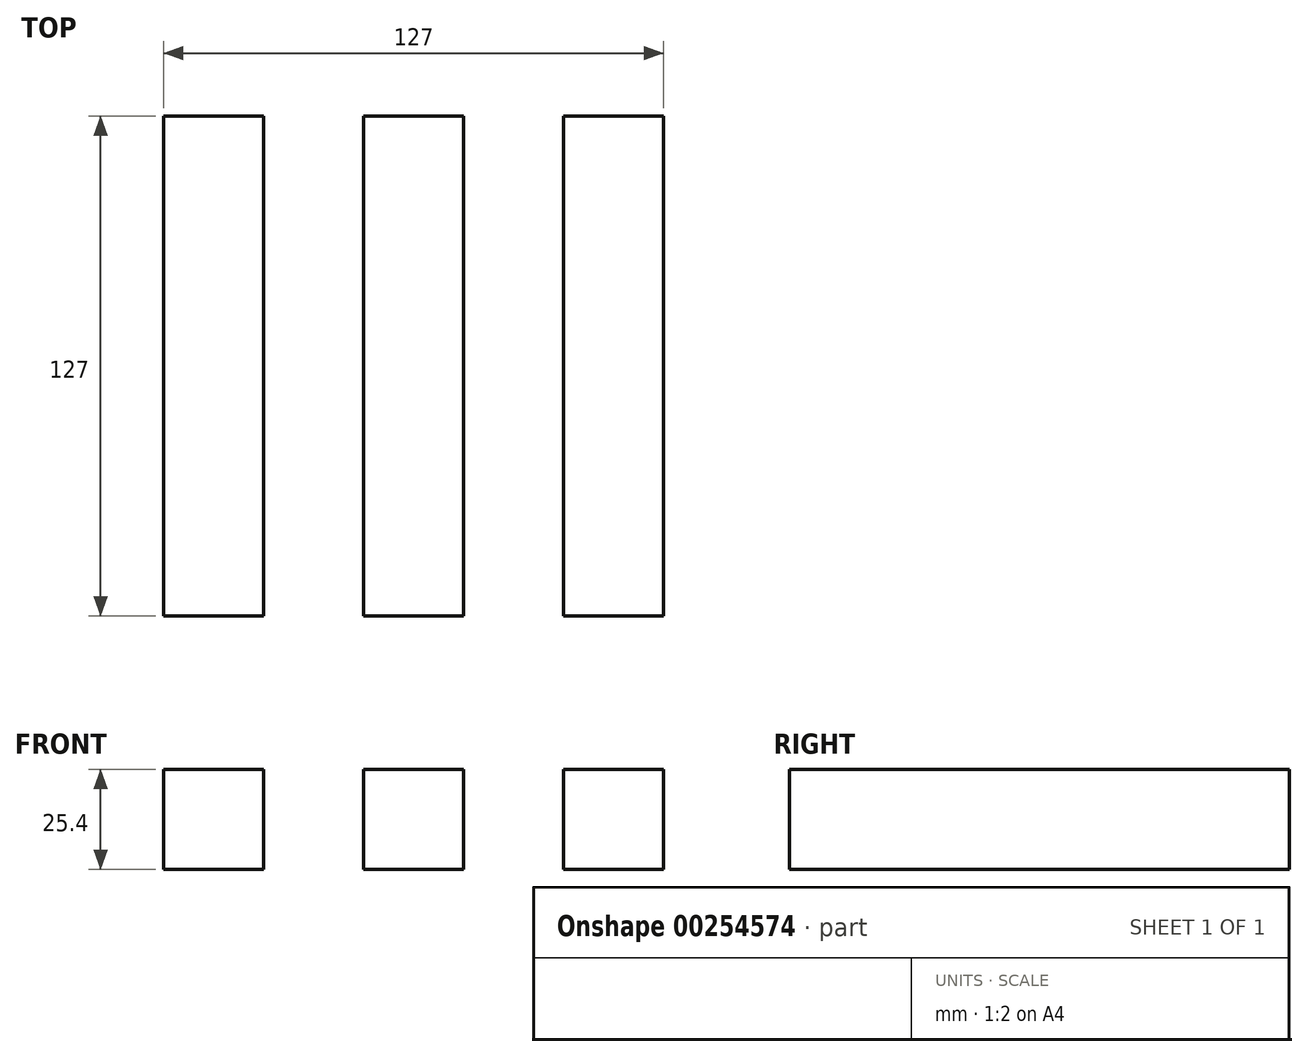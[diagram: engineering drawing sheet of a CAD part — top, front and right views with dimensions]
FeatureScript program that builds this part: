
annotation { "Feature Type Name" : "Feature", "Feature Type Description" : "" }
export const myFeature = defineFeature(function(context is Context, id is Id, definition is map)
    precondition{}
    {
        {
            var Q0;
            Q0=qCreatedBy(makeId("Front.planeOp"),FACE);
            var sketch = newSketch(context, id + "F0", { "sketchPlane" : qUnion([Q0])});
            skLineSegment(sketch, "E0.bottom", {"start": v(12.7, 12.7) * mm, "end": v(-12.7, 12.7) * mm});
            skLineSegment(sketch, "E0.top", {"start": v(12.7, -12.7) * mm, "end": v(-12.7, -12.7) * mm});
            skLineSegment(sketch, "E0.left", {"start": v(12.7, 12.7) * mm, "end": v(12.7, -12.7) * mm});
            skLineSegment(sketch, "E0.right", {"start": v(-12.7, 12.7) * mm, "end": v(-12.7, -12.7) * mm});
            skPoint(sketch, "E0.middle", {"position": v(0, 0) * mm});
            skLineSegment(sketch, "E1", {"start": v(0, 0) * mm, "end": v(-50.8, 0) * mm});
            skLineSegment(sketch, "E2", {"start": v(0, 0) * mm, "end": v(50.8, 0) * mm});
            skLineSegment(sketch, "E3.bottom", {"start": v(-63.5, 12.7) * mm, "end": v(-38.1, 12.7) * mm});
            skLineSegment(sketch, "E3.top", {"start": v(-63.5, -12.7) * mm, "end": v(-38.1, -12.7) * mm});
            skLineSegment(sketch, "E3.left", {"start": v(-63.5, 12.7) * mm, "end": v(-63.5, -12.7) * mm});
            skLineSegment(sketch, "E3.right", {"start": v(-38.1, 12.7) * mm, "end": v(-38.1, -12.7) * mm});
            skPoint(sketch, "E3.middle", {"position": v(-50.8, 0) * mm});
            skLineSegment(sketch, "E4.bottom", {"start": v(63.5, 12.7) * mm, "end": v(38.1, 12.7) * mm});
            skLineSegment(sketch, "E4.top", {"start": v(63.5, -12.7) * mm, "end": v(38.1, -12.7) * mm});
            skLineSegment(sketch, "E4.left", {"start": v(63.5, 12.7) * mm, "end": v(63.5, -12.7) * mm});
            skLineSegment(sketch, "E4.right", {"start": v(38.1, 12.7) * mm, "end": v(38.1, -12.7) * mm});
            skPoint(sketch, "E4.middle", {"position": v(50.8, 0) * mm});
            skSolve(sketch);
        }
        {
            var Q0;
            Q0 = qSketchRegion(id + "F0", true);
            extrude(context, id + "F1", {"entities" : qUnion([Q0]), "endBound" : BoundingType.SYMMETRIC, "depth" : 127 * mm});
        }
    });
